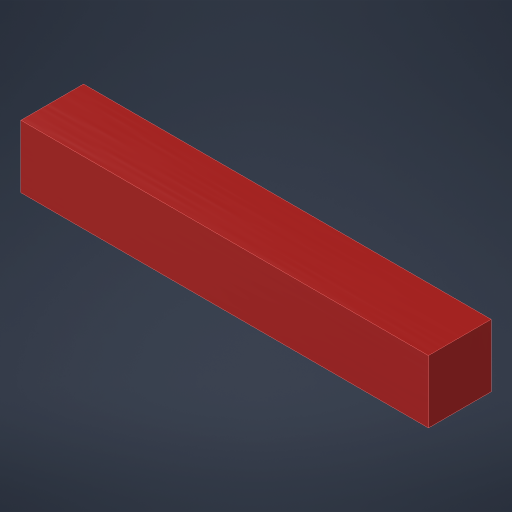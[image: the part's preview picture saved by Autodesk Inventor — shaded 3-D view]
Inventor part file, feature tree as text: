
AUTODESK INVENTOR PART (.ipt)
format: ipt  version: 2024.2 (Build 282272000, 272)  size: 163,328 bytes
history: native  units: in
note: dims shown in document units (in); Inventor stores cm internally (conversion verified against a paired STEP export)
features: extrude x1, sketch x1
ambient origin geometry x8: Origin, YZ Plane, XZ Plane, XY Plane, X Axis, Y Axis, Z Axis, Center Point
bodies: Solid1 (feature_tree)
feature tree (2):
  extrude  "Extrusion1"  Depth=26.0in
  sketch  "Sketch1"  dims[d0=4.0in d1=26.0in d2=4.0in d3=0.0in]
